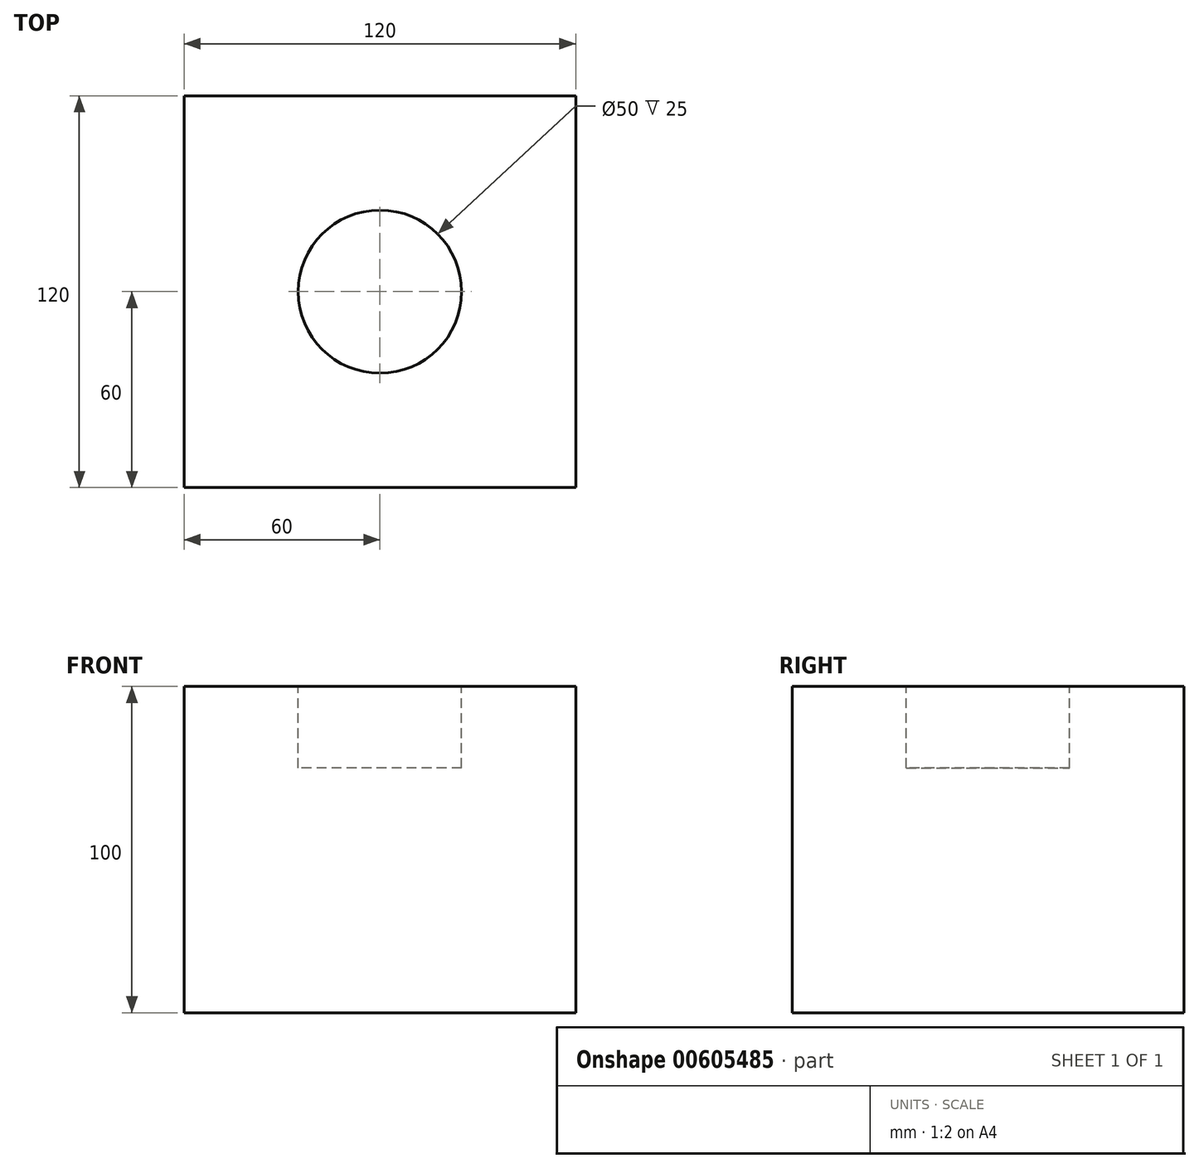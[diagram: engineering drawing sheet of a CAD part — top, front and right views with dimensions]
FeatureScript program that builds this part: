
annotation { "Feature Type Name" : "Feature", "Feature Type Description" : "" }
export const myFeature = defineFeature(function(context is Context, id is Id, definition is map)
    precondition{}
    {
        {
            var Q0;
            Q0=qCreatedBy(makeId("Top.planeOp"),FACE);
            var sketch = newSketch(context, id + "F0", { "sketchPlane" : qUnion([Q0])});
            skLineSegment(sketch, "E0.bottom", {"start": v(60, 60) * mm, "end": v(-60, 60) * mm});
            skLineSegment(sketch, "E0.top", {"start": v(60, -60) * mm, "end": v(-60, -60) * mm});
            skLineSegment(sketch, "E0.left", {"start": v(60, 60) * mm, "end": v(60, -60) * mm});
            skLineSegment(sketch, "E0.right", {"start": v(-60, 60) * mm, "end": v(-60, -60) * mm});
            skPoint(sketch, "E0.middle", {"position": v(0, 0) * mm});
            skSolve(sketch);
        }
        {
            var Q0;
            Q0 = qSketchRegion(id + "F0", true);
            extrude(context, id + "F1", {"entities" : qUnion([Q0]), "depth" : 100 * mm, "offsetDistance" : 25 * mm});
        }
        {
            var Q0;
            Q0=makeQuery(id+"F1.opExtrude","CAP_FACE",FACE,{"disambiguationData":[OSD([sQuery(id+"F0.wireOp",EDGE,"E0.bottom"),sQuery(id+"F0.wireOp",EDGE,"E0.top"),sQuery(id+"F0.wireOp",EDGE,"E0.left"),sQuery(id+"F0.wireOp",EDGE,"E0.right")])],"isStart":false});
            var sketch = newSketch(context, id + "F2", { "sketchPlane" : qUnion([Q0])});
            skCircle(sketch, "E1", {"center": v(0, 0) * mm, "radius": 25 * mm});
            skSolve(sketch);
        }
        {
            var Q0;
            Q0=makeQuery(id+"F2.imprint","IMPRINT",FACE,{"disambiguationData":[TD([[makeQuery(id+"F2.imprint","IMPRINT",EDGE,{"derivedFrom":sQuery(id+"F2.wireOp",EDGE,"E1")}),1.0]])]});
            extrude(context, id + "F3", {"entities" : qUnion([Q0]), "oppositeDirection" : true, "depth" : 25 * mm, "offsetDistance" : 25 * mm});
        }
        {
            var Q0;
            Q0=makeQuery(id+"F3.opExtrude","SWEPT_BODY",BODY,{"disambiguationData":[OSD([sQuery(id+"F2.wireOp",EDGE,"E1")])]});
            var Q1;
            Q1=makeQuery(id+"F1.opExtrude","SWEPT_BODY",BODY,{"disambiguationData":[OSD([sQuery(id+"F0.wireOp",EDGE,"E0.bottom"),sQuery(id+"F0.wireOp",EDGE,"E0.top"),sQuery(id+"F0.wireOp",EDGE,"E0.left"),sQuery(id+"F0.wireOp",EDGE,"E0.right")])]});
            booleanBodies(context, id + "F4", {"operationType" : BooleanOperationType.SUBTRACTION, "tools" : qUnion([Q0]), "targets" : qUnion([Q1])});
        }
    });
